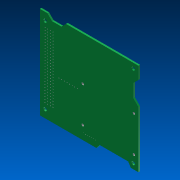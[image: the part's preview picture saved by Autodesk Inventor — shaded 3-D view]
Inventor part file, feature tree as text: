
AUTODESK INVENTOR PART (.ipt)
format: ipt  version: 2012 (Build 160160000, 160)  size: 578,560 bytes
history: native  units: in
note: dims shown in document units (in); Inventor stores cm internally (conversion verified against a paired STEP export)
features: other x2, sketch x1, extrude x1, imported_body x1
ambient origin geometry x8: Origin, YZ Plane, XZ Plane, XY Plane, X Axis, Y Axis, Z Axis, Center Point
feature tree (5):
  other  "Sólido1"
  other  "placa_pc1041"
  sketch  "Sketch3"  dims[d7=0.0315in d8=0.0in]
  extrude  "Extrusion2"  [1 undecoded]
  imported_body  "Base1"
note: 1 required parameter value undecoded (feature->parameter linkage not recoverable at this tier; creation-order binding heuristic only, values carry confidence <= 0.55)
